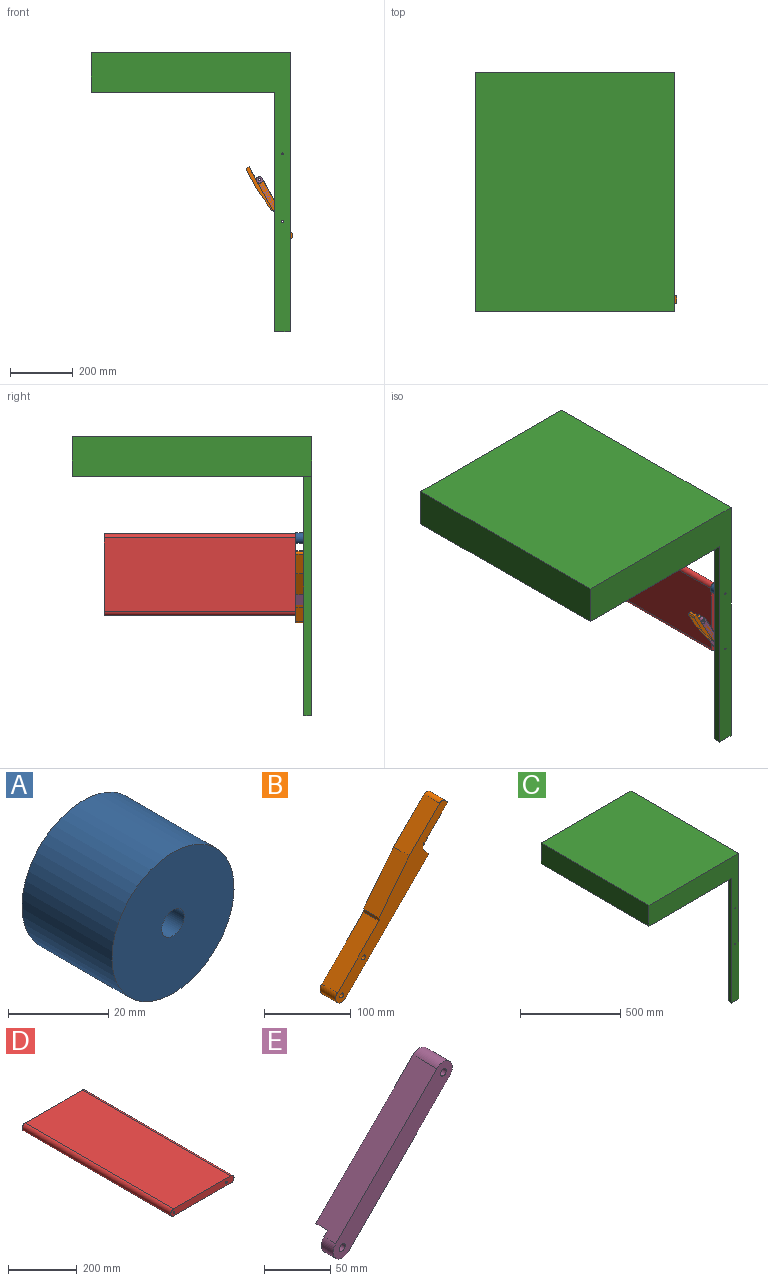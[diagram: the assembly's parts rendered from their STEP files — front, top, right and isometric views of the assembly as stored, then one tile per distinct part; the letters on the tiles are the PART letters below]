
ASSEMBLY  parts=5 mates=5
PART A: 4 faces, bbox 34.5x25.4x34.5 mm
  f0: cylinder r=17.23mm len=34.46mm, axis (0,-1,0), area 2749.5mm2, adj f1,f2
  f1: plane 34.46x34.46mm, normal (0,1,0), area 900.8mm2, adj f0,f3
  f2: plane 34.46x34.46mm, normal (0,-1,0), area 900.8mm2, adj f0,f3
  f3: cylinder r=3.17mm len=25.4mm, axis (0,-1,0), area 506.7mm2, adj f1,f2
PART B: 18 faces, bbox 183.1x25.4x202.9 mm
  f0: plane 36.63x36.63mm, normal (0.71,0,-0.71), area 1243.1mm2, adj f6,f7,f10,f11,f13,f14
  f1: plane 68.06x68.06mm, normal (-0.71,0,0.71), area 2444.6mm2, adj f2,f9,f10,f11
  f2: plane 25.4x4.22mm, normal (-1,0,0), area 107.2mm2, adj f1,f3,f10,f11
  f3: plane 63.02x49.28mm, normal (-0.79,0,0.62), area 2032mm2, adj f2,f4,f10,f11
  f4: plane 49.51x49.51mm, normal (-0.71,0,0.71), area 1778.5mm2, adj f3,f5,f10,f11
  f5: cylinder r=6.35mm len=25.4mm, axis (0,-1,0), area 253.4mm2, adj f4,f6,f10,f11
  f6: plane 25.4x4.49mm, normal (0.71,0,0.71), area 161.3mm2, adj f0,f5,f10,f11
  f7: cylinder r=9.53mm len=16.26mm, axis (0,-1,0), area 380mm2, adj f0,f8,f10,f14
  f8: plane 143.68x143.68mm, normal (0.71,0,-0.71), area 5020.2mm2, adj f7,f9,f10,f11,f12,f14
  f9: cylinder r=9.53mm len=25.4mm, axis (0,-1,0), area 760.1mm2, adj f1,f8,f10,f11
  f10: plane 202.92x183.1mm, normal (0,1,0), area 5649.3mm2, adj f0,f1,f2,f3,f4,f5,f6,f7
  f11: plane 202.92x183.1mm, normal (0,-1,0), area 5329.5mm2, adj f0,f1,f2,f3,f4,f5,f6,f8
  f12: plane 12.7x6.74mm, normal (0.71,0,0.71), area 121mm2, adj f8,f11,f13,f14
  f13: cylinder r=11.11mm len=18.64mm, axis (0,-1,0), area 298mm2, adj f0,f11,f12,f14
  f14: plane 25.38x20.64mm, normal (0,-1,0), area 319.8mm2, adj f0,f7,f8,f12,f13,f15
  f15: cylinder r=3.17mm len=12.7mm, axis (0,-1,0), area 253.4mm2, adj f10,f14
  f16: cylinder r=3.17mm len=25.4mm, axis (0,-1,0), area 506.7mm2, adj f10,f11
  f17: cylinder r=3.17mm len=25.4mm, axis (0,-1,0), area 506.7mm2, adj f10,f11
PART C: 11 faces, bbox 635x762x889 mm
  f0: plane 762x635mm, normal (0,0,-1), area 482579.7mm2, adj f1,f3,f4,f5,f6,f8
  f1: plane 889x762mm, normal (1,0,0), area 116128.8mm2, adj f0,f2,f4,f5,f7,f8
  f2: plane 762x635mm, normal (0,0,1), area 483870mm2, adj f1,f3,f4,f5
  f3: plane 762x127mm, normal (-1,0,0), area 96774mm2, adj f0,f2,f4,f5
  f4: plane 635x127mm, normal (0,1,0), area 80645mm2, adj f0,f1,f2,f3
  f5: plane 889x635mm, normal (0,-1,0), area 119291.3mm2, adj f0,f1,f2,f3,f6,f7,f9,f10
  f6: plane 762x25.4mm, normal (-1,0,0), area 19354.8mm2, adj f0,f5,f7,f8
  f7: plane 50.8x25.4mm, normal (0,0,-1), area 1290.3mm2, adj f1,f5,f6,f8
  f8: plane 762x50.8mm, normal (0,1,0), area 38646.3mm2, adj f0,f1,f6,f7,f9,f10
  f9: cylinder r=3.17mm len=25.4mm, axis (0,1,0), area 506.7mm2, adj f5,f8
  f10: cylinder r=3.17mm len=25.4mm, axis (0,1,0), area 506.7mm2, adj f5,f8
PART D: 8 faces, bbox 259.5x609.6x25.4 mm
  f0: plane 609.6x234.07mm, normal (0,0,1), area 142689.2mm2, adj f1,f3,f5,f6
  f1: cylinder r=12.7mm len=609.6mm, axis (0,-1,0), area 24322mm2, adj f0,f2,f5,f6
  f2: plane 609.6x234.07mm, normal (0,0,-1), area 142689.2mm2, adj f1,f3,f5,f6
  f3: cylinder r=12.7mm len=609.6mm, axis (0,-1,0), area 24322mm2, adj f0,f2,f5,f6
  f4: cylinder r=3.17mm len=609.6mm, axis (0,-1,0), area 12161mm2, adj f5,f6
  f5: plane 259.47x25.4mm, normal (0,1,0), area 6388.8mm2, adj f0,f1,f2,f3,f4,f7
  f6: plane 259.47x25.4mm, normal (0,-1,0), area 6388.8mm2, adj f0,f1,f2,f3,f4,f7
  f7: cylinder r=3.17mm len=609.6mm, axis (0,-1,0), area 12161mm2, adj f5,f6
PART E: 11 faces, bbox 126.8x25.4x126.8 mm
  f0: plane 107.76x107.76mm, normal (0.71,0,-0.71), area 3729.8mm2, adj f2,f3,f4,f5,f6,f8
  f1: plane 107.76x107.76mm, normal (-0.71,0,0.71), area 3798.3mm2, adj f2,f3,f4,f5,f6,f7
  f2: cylinder r=9.53mm len=25.4mm, axis (0,-1,0), area 760.1mm2, adj f0,f1,f3,f4
  f3: plane 119.98x116.17mm, normal (0,1,0), area 2817.4mm2, adj f0,f1,f2,f7,f8,f10
  f4: plane 126.81x126.81mm, normal (0,-1,0), area 3124.9mm2, adj f0,f1,f2,f5,f9,f10
  f5: cylinder r=9.53mm len=16.26mm, axis (0,-1,0), area 380mm2, adj f0,f1,f4,f6
  f6: plane 24.12x20.64mm, normal (0,1,0), area 307.5mm2, adj f0,f1,f5,f7,f8,f9
  f7: cylinder r=11.11mm len=12.7mm, axis (0,1,0), area 145.3mm2, adj f1,f3,f6,f8
  f8: plane 12.7x6.74mm, normal (-0.71,0,-0.71), area 121mm2, adj f0,f3,f6,f7
  f9: cylinder r=3.17mm len=12.7mm, axis (0,-1,0), area 253.4mm2, adj f4,f6
  f10: cylinder r=3.17mm len=25.4mm, axis (0,-1,0), area 506.7mm2, adj f3,f4
PLACE A t=(119.6,-324.12,178.64)mm
PLACE B rot(axis=(0,-1,0),73.6deg) t=(-293.8,-324.12,-92.73)mm
PLACE C t=(119.6,-324.12,178.64)mm fixed
PLACE D rot(axis=(0,1,0),90deg) t=(290.55,-324.12,-43.11)mm
PLACE E rot(axis=(0,1,0),106.4deg) t=(336.19,-324.12,-106.2)mm
MATE revolute E.f5 <-> B.f7  axis (0,1,0) through (21.19,-286.02,-99.46)mm
MATE revolute A.f0 <-> D.f3  axis (0,1,0) through (94.2,-273.32,-17.71)mm
MATE revolute C.f9 <-> B.f17  axis (0,1,0) through (94.2,-298.72,-233.24)mm
MATE fastened A.f0 <-> C.f10  axis (0,-1,0) through (94.2,-298.72,-17.71)mm
MATE revolute D.f7 <-> E.f2  axis (0,-1,0) through (94.2,-273.32,-233.24)mm
